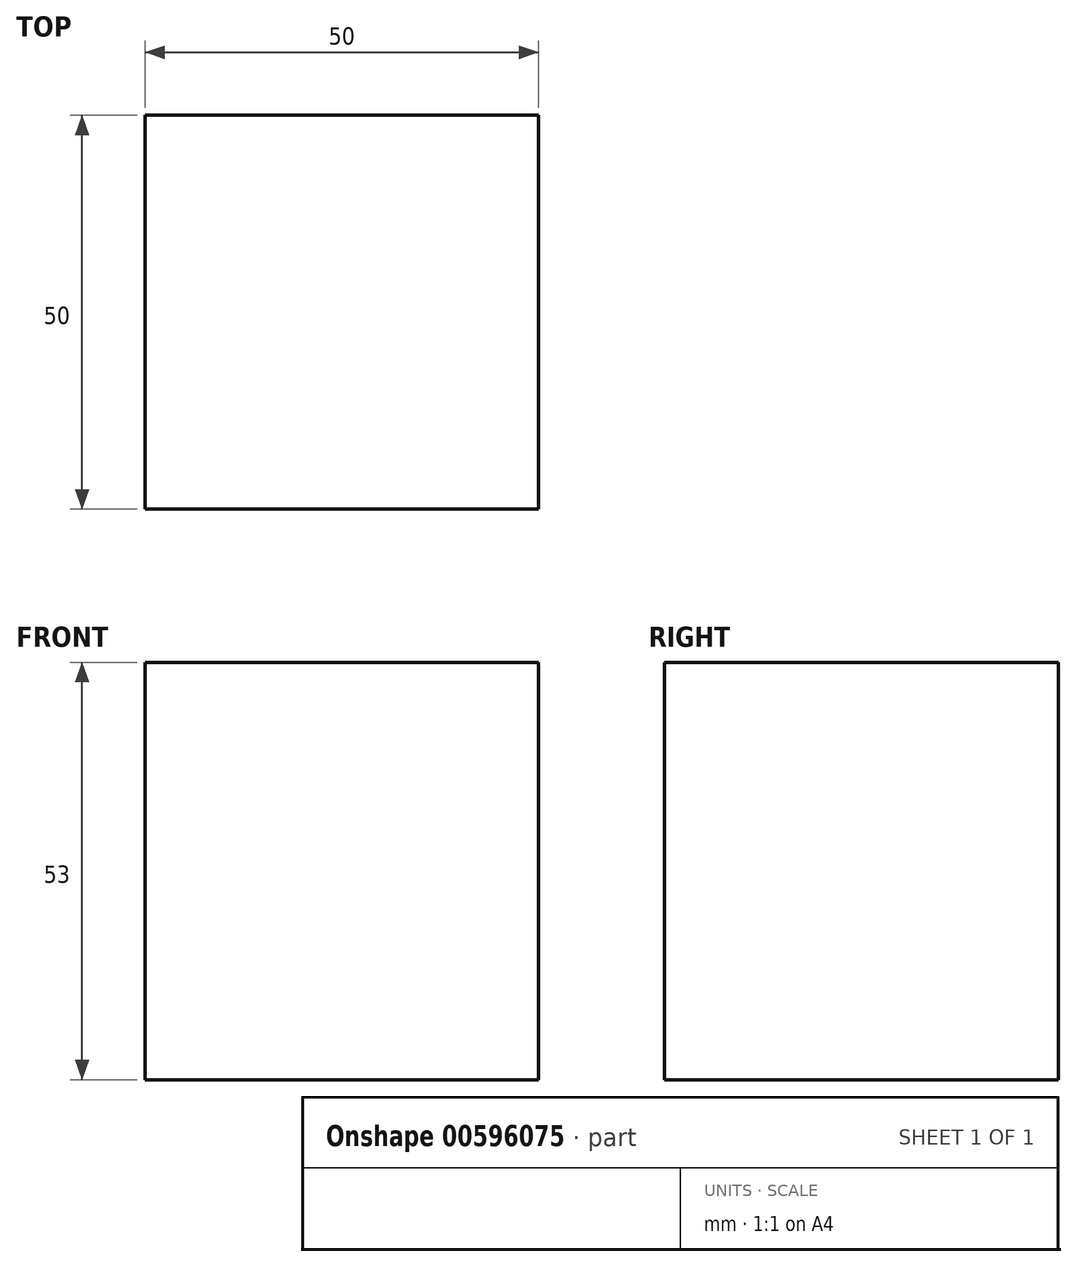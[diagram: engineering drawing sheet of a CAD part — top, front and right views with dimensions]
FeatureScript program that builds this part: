
annotation { "Feature Type Name" : "Feature", "Feature Type Description" : "" }
export const myFeature = defineFeature(function(context is Context, id is Id, definition is map)
    precondition{}
    {
        {
            var Q0;
            Q0=qCreatedBy(makeId("Top.planeOp"),FACE);
            var sketch = newSketch(context, id + "F0", { "sketchPlane" : qUnion([Q0])});
            skLineSegment(sketch, "E0.bottom", {"start": v(-25, 25) * mm, "end": v(25, 25) * mm});
            skLineSegment(sketch, "E0.top", {"start": v(-25, -25) * mm, "end": v(25, -25) * mm});
            skLineSegment(sketch, "E0.left", {"start": v(-25, 25) * mm, "end": v(-25, -25) * mm});
            skLineSegment(sketch, "E0.right", {"start": v(25, 25) * mm, "end": v(25, -25) * mm});
            skPoint(sketch, "E0.middle", {"position": v(0, 0) * mm});
            skSolve(sketch);
        }
        {
            var Q0;
            Q0 = qSketchRegion(id + "F0", true);
            extrude(context, id + "F1", {"entities" : qUnion([Q0]), "depth" : 53 * mm, "offsetDistance" : 25 * mm});
        }
    });
